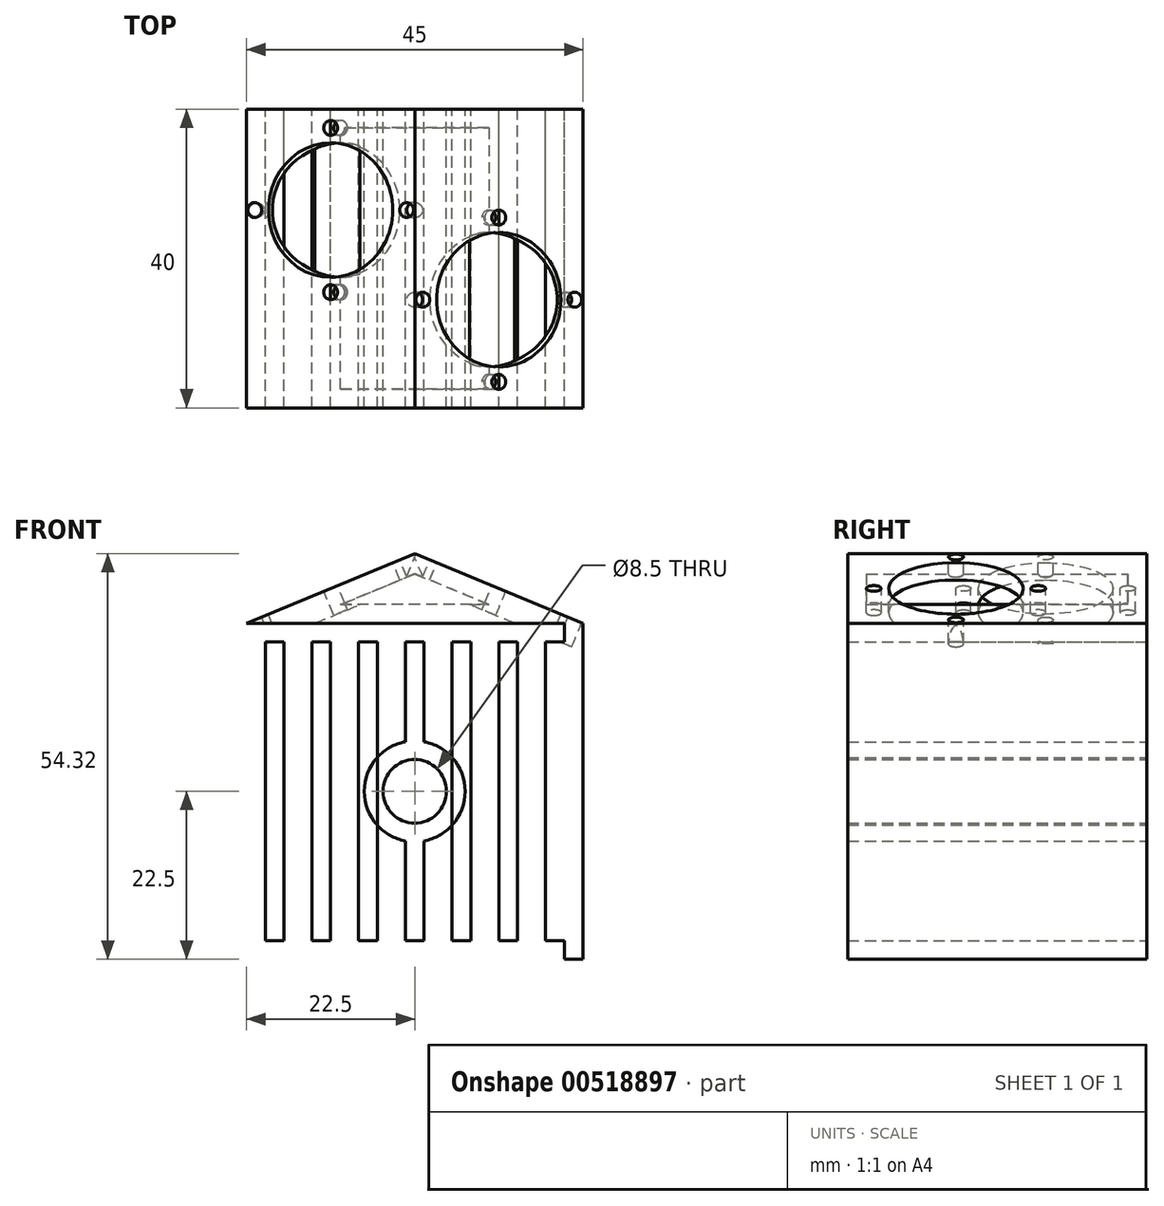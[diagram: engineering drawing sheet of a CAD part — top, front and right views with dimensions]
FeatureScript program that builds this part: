
annotation { "Feature Type Name" : "Feature", "Feature Type Description" : "" }
export const myFeature = defineFeature(function(context is Context, id is Id, definition is map)
    precondition{}
    {
        {
            var Q0;
            Q0=qCreatedBy(makeId("Front.planeOp"),FACE);
            var sketch = newSketch(context, id + "F0", { "sketchPlane" : qUnion([Q0])});
            skLineSegment(sketch, "E0.bottom", {"start": v(22.5, 22.5) * mm, "end": v(-22.5, 22.5) * mm});
            skLineSegment(sketch, "E0.top", {"start": v(22.5, -22.5) * mm, "end": v(-22.5, -22.5) * mm});
            skLineSegment(sketch, "E0.left", {"start": v(22.5, 22.5) * mm, "end": v(22.5, -22.5) * mm});
            skLineSegment(sketch, "E0.right", {"start": v(-22.5, 22.5) * mm, "end": v(-22.5, -22.5) * mm});
            skPoint(sketch, "E0.middle", {"position": v(0, 0) * mm});
            skLineSegment(sketch, "E1", {"start": v(-22.5, 22.5) * mm, "end": v(0, 31.82) * mm});
            skLineSegment(sketch, "E2", {"start": v(0, 31.82) * mm, "end": v(22.5, 22.5) * mm});
            skCircle(sketch, "E3", {"center": v(0, 0) * mm, "radius": 4.25 * mm});
            skLineSegment(sketch, "E4.bottom", {"start": v(22.5, 22.5) * mm, "end": v(20, 22.5) * mm});
            skLineSegment(sketch, "E4.top", {"start": v(22.5, 20) * mm, "end": v(20, 20) * mm});
            skLineSegment(sketch, "E4.left", {"start": v(22.5, 22.5) * mm, "end": v(22.5, 20) * mm});
            skLineSegment(sketch, "E4.right", {"start": v(20, 22.5) * mm, "end": v(20, 20) * mm});
            skLineSegment(sketch, "E5.bottom", {"start": v(22.5, -22.5) * mm, "end": v(20, -22.5) * mm});
            skLineSegment(sketch, "E5.top", {"start": v(22.5, -20) * mm, "end": v(20, -20) * mm});
            skLineSegment(sketch, "E5.left", {"start": v(22.5, -22.5) * mm, "end": v(22.5, -20) * mm});
            skLineSegment(sketch, "E5.right", {"start": v(20, -22.5) * mm, "end": v(20, -20) * mm});
            skPoint(sketch, "E6.oppositeSnap0", {"position": v(21.25, -20) * mm});
            skLineSegment(sketch, "E6.bottom", {"start": v(20, 20) * mm, "end": v(17.5, 20) * mm});
            skLineSegment(sketch, "E6.top", {"start": v(20, -20) * mm, "end": v(17.5, -20) * mm});
            skLineSegment(sketch, "E6.left", {"start": v(20, 20) * mm, "end": v(20, -20) * mm});
            skLineSegment(sketch, "E6.right", {"start": v(17.5, 20) * mm, "end": v(17.5, -20) * mm});
            skLineSegment(sketch, "E7.1.0.0", {"start": v(13.75, 20) * mm, "end": v(13.75, -20) * mm});
            skLineSegment(sketch, "E7.1.0.1", {"start": v(11.25, 20) * mm, "end": v(11.25, -20) * mm});
            skLineSegment(sketch, "E7.1.0.2", {"start": v(13.75, 20) * mm, "end": v(11.25, 20) * mm});
            skLineSegment(sketch, "E7.1.0.3", {"start": v(13.75, -20) * mm, "end": v(11.25, -20) * mm});
            skLineSegment(sketch, "E7.2.0.0", {"start": v(7.5, 20) * mm, "end": v(7.5, -20) * mm});
            skLineSegment(sketch, "E7.2.0.1", {"start": v(5, 20) * mm, "end": v(5, -20) * mm});
            skLineSegment(sketch, "E7.2.0.2", {"start": v(7.5, 20) * mm, "end": v(5, 20) * mm});
            skLineSegment(sketch, "E7.2.0.3", {"start": v(7.5, -20) * mm, "end": v(5, -20) * mm});
            skLineSegment(sketch, "E7.3.0.0", {"start": v(1.25, 20) * mm, "end": v(1.25, -20) * mm});
            skLineSegment(sketch, "E7.3.0.1", {"start": v(-1.25, 20) * mm, "end": v(-1.25, -20) * mm});
            skLineSegment(sketch, "E7.3.0.2", {"start": v(1.25, 20) * mm, "end": v(-1.25, 20) * mm});
            skLineSegment(sketch, "E7.3.0.3", {"start": v(1.25, -20) * mm, "end": v(-1.25, -20) * mm});
            skLineSegment(sketch, "E7.4.0.0", {"start": v(-5, 20) * mm, "end": v(-5, -20) * mm});
            skLineSegment(sketch, "E7.4.0.1", {"start": v(-7.5, 20) * mm, "end": v(-7.5, -20) * mm});
            skLineSegment(sketch, "E7.4.0.2", {"start": v(-5, 20) * mm, "end": v(-7.5, 20) * mm});
            skLineSegment(sketch, "E7.4.0.3", {"start": v(-5, -20) * mm, "end": v(-7.5, -20) * mm});
            skLineSegment(sketch, "E7.5.0.0", {"start": v(-11.25, 20) * mm, "end": v(-11.25, -20) * mm});
            skLineSegment(sketch, "E7.5.0.1", {"start": v(-13.75, 20) * mm, "end": v(-13.75, -20) * mm});
            skLineSegment(sketch, "E7.5.0.2", {"start": v(-11.25, 20) * mm, "end": v(-13.75, 20) * mm});
            skLineSegment(sketch, "E7.5.0.3", {"start": v(-11.25, -20) * mm, "end": v(-13.75, -20) * mm});
            skLineSegment(sketch, "E7.direction1", {"start": v(20, -20) * mm, "end": v(13.75, -20) * mm, "construction": true});
            skCircle(sketch, "E8", {"center": v(0, 0) * mm, "radius": 6.75 * mm});
            skLineSegment(sketch, "E9.0.6.0", {"start": v(-17.5, 20) * mm, "end": v(-17.5, -20) * mm});
            skLineSegment(sketch, "E9.3.6.0", {"start": v(-20, 20) * mm, "end": v(-20, -20) * mm});
            skLineSegment(sketch, "E9.6.6.0", {"start": v(-17.5, 20) * mm, "end": v(-20, 20) * mm});
            skLineSegment(sketch, "E9.9.6.0", {"start": v(-17.5, -20) * mm, "end": v(-20, -20) * mm});
            skSolve(sketch);
        }
        {
            var Q0;
            {var subQ0=sQuery(id+"F0.wireOp",EDGE,"E7.3.0.1");var subQ1=sQuery(id+"F0.wireOp",EDGE,"E3");var subQ2=makeQuery(id+"F0.imprint","INTERSECT",VERTEX,{"disambiguationData":[OD(0.0)],"derivedFrom":[subQ1,subQ0]});Q0=makeQuery(id+"F0.imprint","IMPRINT",FACE,{"disambiguationData":[TD([[makeQuery(id+"F0.imprint","IMPRINT",EDGE,{"disambiguationData":[TD([[subQ2,-1.0]])],"derivedFrom":subQ1}),1.0]])]});}
            var Q1;
            {var subQ0=sQuery(id+"F0.wireOp",EDGE,"E7.3.0.0");var subQ1=sQuery(id+"F0.wireOp",EDGE,"E3");var subQ2=makeQuery(id+"F0.imprint","INTERSECT",VERTEX,{"disambiguationData":[OD(0.0)],"derivedFrom":[subQ1,subQ0]});Q1=makeQuery(id+"F0.imprint","IMPRINT",FACE,{"disambiguationData":[TD([[makeQuery(id+"F0.imprint","IMPRINT",EDGE,{"disambiguationData":[TD([[subQ2,1.0]])],"derivedFrom":subQ1}),1.0]])]});}
            var Q2;
            Q2=makeQuery(id+"F0.imprint","IMPRINT",FACE,{"disambiguationData":[TD([[makeQuery(id+"F0.imprint","IMPRINT",EDGE,{"derivedFrom":sQuery(id+"F0.wireOp",EDGE,"E7.5.0.0")}),-1.0]])]});
            var Q3;
            Q3=makeQuery(id+"F0.imprint","IMPRINT",FACE,{"disambiguationData":[TD([[makeQuery(id+"F0.imprint","IMPRINT",EDGE,{"derivedFrom":sQuery(id+"F0.wireOp",EDGE,"E6.bottom")}),1.0]])]});
            var Q4;
            Q4=makeQuery(id+"F0.imprint","IMPRINT",FACE,{"disambiguationData":[TD([[makeQuery(id+"F0.imprint","IMPRINT",EDGE,{"derivedFrom":sQuery(id+"F0.wireOp",EDGE,"E7.2.0.0")}),-1.0]])]});
            var Q5;
            {var subQ0=sQuery(id+"F0.wireOp",EDGE,"E8");var subQ1=sQuery(id+"F0.wireOp",EDGE,"E7.2.0.1");var subQ2=makeQuery(id+"F0.imprint","INTERSECT",VERTEX,{"disambiguationData":[OD(0.0)],"derivedFrom":[subQ1,subQ0]});Q5=makeQuery(id+"F0.imprint","IMPRINT",FACE,{"disambiguationData":[TD([[makeQuery(id+"F0.imprint","IMPRINT",EDGE,{"disambiguationData":[TD([[subQ2,-1.0]])],"derivedFrom":subQ1}),1.0]])]});}
            var Q6;
            {var subQ0=sQuery(id+"F0.wireOp",EDGE,"E7.3.0.2");Q6=makeQuery(id+"F0.imprint","IMPRINT",FACE,{"disambiguationData":[TD([[makeQuery(id+"F0.imprint","IMPRINT",EDGE,{"derivedFrom":subQ0}),1.0]])]});}
            var Q7;
            {var subQ4=sQuery(id+"F0.wireOp",EDGE,"E7.3.0.1");var subQ6=sQuery(id+"F0.wireOp",EDGE,"E3");var subQ9=makeQuery(id+"F0.imprint","INTERSECT",VERTEX,{"disambiguationData":[OD(0.0)],"derivedFrom":[subQ6,subQ4]});Q7=makeQuery(id+"F0.imprint","IMPRINT",FACE,{"disambiguationData":[TD([[makeQuery(id+"F0.imprint","IMPRINT",EDGE,{"disambiguationData":[TD([[subQ9,-1.0]])],"derivedFrom":subQ6}),-1.0]])]});}
            var Q8;
            {var subQ0=sQuery(id+"F0.wireOp",EDGE,"E7.3.0.1");var subQ1=sQuery(id+"F0.wireOp",EDGE,"E3");var subQ2=makeQuery(id+"F0.imprint","INTERSECT",VERTEX,{"disambiguationData":[OD(1.0)],"derivedFrom":[subQ1,subQ0]});Q8=makeQuery(id+"F0.imprint","IMPRINT",FACE,{"disambiguationData":[TD([[makeQuery(id+"F0.imprint","IMPRINT",EDGE,{"disambiguationData":[TD([[subQ2,-1.0]])],"derivedFrom":subQ1}),-1.0]])]});}
            var Q9;
            {var subQ0=sQuery(id+"F0.wireOp",EDGE,"E7.3.0.0");var subQ1=sQuery(id+"F0.wireOp",EDGE,"E3");var subQ5=makeQuery(id+"F0.imprint","INTERSECT",VERTEX,{"disambiguationData":[OD(0.0)],"derivedFrom":[subQ1,subQ0]});Q9=makeQuery(id+"F0.imprint","IMPRINT",FACE,{"disambiguationData":[TD([[makeQuery(id+"F0.imprint","IMPRINT",EDGE,{"disambiguationData":[TD([[subQ5,1.0]])],"derivedFrom":subQ1}),-1.0]])]});}
            var Q10;
            {var subQ0=sQuery(id+"F0.wireOp",EDGE,"E7.3.0.1");var subQ1=sQuery(id+"F0.wireOp",EDGE,"E3");var subQ2=makeQuery(id+"F0.imprint","INTERSECT",VERTEX,{"disambiguationData":[OD(0.0)],"derivedFrom":[subQ1,subQ0]});Q10=makeQuery(id+"F0.imprint","IMPRINT",FACE,{"disambiguationData":[TD([[makeQuery(id+"F0.imprint","IMPRINT",EDGE,{"disambiguationData":[TD([[subQ2,1.0]])],"derivedFrom":subQ1}),-1.0]])]});}
            var Q11;
            {var subQ0=sQuery(id+"F0.wireOp",EDGE,"E8");var subQ1=sQuery(id+"F0.wireOp",EDGE,"E7.4.0.0");var subQ2=makeQuery(id+"F0.imprint","INTERSECT",VERTEX,{"disambiguationData":[OD(0.0)],"derivedFrom":[subQ1,subQ0]});Q11=makeQuery(id+"F0.imprint","IMPRINT",FACE,{"disambiguationData":[TD([[makeQuery(id+"F0.imprint","IMPRINT",EDGE,{"disambiguationData":[TD([[subQ2,-1.0]])],"derivedFrom":subQ1}),-1.0]])]});}
            var Q12;
            Q12=makeQuery(id+"F0.imprint","IMPRINT",FACE,{"disambiguationData":[TD([[makeQuery(id+"F0.imprint","IMPRINT",EDGE,{"derivedFrom":sQuery(id+"F0.wireOp",EDGE,"E7.4.0.1")}),1.0]])]});
            var Q13;
            Q13=makeQuery(id+"F0.imprint","IMPRINT",FACE,{"disambiguationData":[TD([[makeQuery(id+"F0.imprint","IMPRINT",EDGE,{"derivedFrom":sQuery(id+"F0.wireOp",EDGE,"E9.0.6.0")}),-1.0]])]});
            var Q14;
            Q14=makeQuery(id+"F0.imprint","IMPRINT",FACE,{"disambiguationData":[TD([[makeQuery(id+"F0.imprint","IMPRINT",EDGE,{"derivedFrom":sQuery(id+"F0.wireOp",EDGE,"E0.bottom")}),-1.0]])]});
            var Q15;
            Q15=makeQuery(id+"F0.imprint","IMPRINT",FACE,{"disambiguationData":[TD([[makeQuery(id+"F0.imprint","IMPRINT",EDGE,{"derivedFrom":sQuery(id+"F0.wireOp",EDGE,"E0.left")}),-1.0]])]});
            var Q16;
            {var subQ0=sQuery(id+"F0.wireOp",EDGE,"E7.3.0.1");var subQ1=sQuery(id+"F0.wireOp",EDGE,"E3");var subQ2=makeQuery(id+"F0.imprint","INTERSECT",VERTEX,{"disambiguationData":[OD(0.0)],"derivedFrom":[subQ1,subQ0]});Q16=makeQuery(id+"F0.imprint","IMPRINT",FACE,{"disambiguationData":[TD([[makeQuery(id+"F0.imprint","IMPRINT",EDGE,{"disambiguationData":[TD([[subQ2,1.0]])],"derivedFrom":subQ1}),1.0]])]});}
            var Q17;
            Q17=makeQuery(id+"F0.imprint","IMPRINT",FACE,{"disambiguationData":[TD([[makeQuery(id+"F0.imprint","IMPRINT",EDGE,{"derivedFrom":sQuery(id+"F0.wireOp",EDGE,"E5.bottom")}),-1.0]])]});
            var Q18;
            {var subQ0=sQuery(id+"F0.wireOp",EDGE,"E7.3.0.3");Q18=makeQuery(id+"F0.imprint","IMPRINT",FACE,{"disambiguationData":[TD([[makeQuery(id+"F0.imprint","IMPRINT",EDGE,{"derivedFrom":subQ0}),-1.0]])]});}
            var Q19;
            Q19=makeQuery(id+"F0.imprint","IMPRINT",FACE,{"disambiguationData":[TD([[makeQuery(id+"F0.imprint","IMPRINT",EDGE,{"derivedFrom":sQuery(id+"F0.wireOp",EDGE,"E7.1.0.0")}),-1.0]])]});
            var Q20;
            Q20=makeQuery(id+"F0.imprint","IMPRINT",FACE,{"disambiguationData":[TD([[makeQuery(id+"F0.imprint","IMPRINT",EDGE,{"derivedFrom":sQuery(id+"F0.wireOp",EDGE,"E0.bottom")}),1.0]])]});
            var Q21;
            Q21=makeQuery(id+"F0.imprint","IMPRINT",FACE,{"disambiguationData":[TD([[makeQuery(id+"F0.imprint","IMPRINT",EDGE,{"derivedFrom":sQuery(id+"F0.wireOp",EDGE,"E4.bottom")}),1.0]])]});
            extrude(context, id + "F1", {"entities" : qUnion([Q0, Q1, Q2, Q3, Q4, Q5, Q6, Q7, Q8, Q9, Q10, Q11, Q12, Q13, Q14, Q15, Q16, Q17, Q18, Q19, Q20, Q21]), "depth" : 40 * mm, "offsetDistance" : 25 * mm});
        }
        {
            var Q0;
            Q0=makeQuery(id+"F1.opExtrude","SWEPT_FACE",FACE,{"disambiguationData":[OSD([sQuery(id+"F0.wireOp",EDGE,"E0.top"),sQuery(id+"F0.wireOp",EDGE,"E5.bottom")])]});
            shell(context, id + "F2", {"entities" : qUnion([Q0]), "thickness" : 2.5 * mm});
        }
        {
            var Q0;
            {var subQ0=sQuery(id+"F0.wireOp",EDGE,"E7.3.0.0");var subQ1=sQuery(id+"F0.wireOp",EDGE,"E3");var subQ2=makeQuery(id+"F0.imprint","INTERSECT",VERTEX,{"disambiguationData":[OD(0.0)],"derivedFrom":[subQ1,subQ0]});Q0=makeQuery(id+"F0.imprint","IMPRINT",FACE,{"disambiguationData":[TD([[makeQuery(id+"F0.imprint","IMPRINT",EDGE,{"disambiguationData":[TD([[subQ2,1.0]])],"derivedFrom":subQ1}),1.0]])]});}
            var Q1;
            {var subQ0=sQuery(id+"F0.wireOp",EDGE,"E7.3.0.1");var subQ1=sQuery(id+"F0.wireOp",EDGE,"E3");var subQ2=makeQuery(id+"F0.imprint","INTERSECT",VERTEX,{"disambiguationData":[OD(0.0)],"derivedFrom":[subQ1,subQ0]});Q1=makeQuery(id+"F0.imprint","IMPRINT",FACE,{"disambiguationData":[TD([[makeQuery(id+"F0.imprint","IMPRINT",EDGE,{"disambiguationData":[TD([[subQ2,1.0]])],"derivedFrom":subQ1}),1.0]])]});}
            var Q2;
            {var subQ0=sQuery(id+"F0.wireOp",EDGE,"E7.3.0.1");var subQ1=sQuery(id+"F0.wireOp",EDGE,"E3");var subQ2=makeQuery(id+"F0.imprint","INTERSECT",VERTEX,{"disambiguationData":[OD(0.0)],"derivedFrom":[subQ1,subQ0]});Q2=makeQuery(id+"F0.imprint","IMPRINT",FACE,{"disambiguationData":[TD([[makeQuery(id+"F0.imprint","IMPRINT",EDGE,{"disambiguationData":[TD([[subQ2,-1.0]])],"derivedFrom":subQ1}),1.0]])]});}
            extrude(context, id + "F3", {"entities" : qUnion([Q0, Q1, Q2]), "operationType" : NewBodyOperationType.REMOVE, "depth" : 40 * mm, "offsetDistance" : 25 * mm});
        }
        {
            var Q0;
            Q0=makeQuery(id+"F1.opExtrude","SWEPT_FACE",FACE,{"disambiguationData":[OSD([sQuery(id+"F0.wireOp",EDGE,"E1")])]});
            var sketch = newSketch(context, id + "F4", { "sketchPlane" : qUnion([Q0])});
            skLineSegment(sketch, "E10", {"start": v(0, 0) * mm, "end": v(0, -13.5) * mm});
            skPoint(sketch, "E10.endSnap0", {"position": v(0, 0) * mm});
            skCircle(sketch, "E11", {"center": v(0, -13.5) * mm, "radius": 9 * mm});
            skLineSegment(sketch, "E12", {"start": v(0, -13.5) * mm, "end": v(-11, -13.5) * mm});
            skLineSegment(sketch, "E13", {"start": v(0, -13.5) * mm, "end": v(0, -24.5) * mm});
            skLineSegment(sketch, "E14", {"start": v(0, -13.5) * mm, "end": v(11, -13.5) * mm});
            skLineSegment(sketch, "E15", {"start": v(0, -13.5) * mm, "end": v(0, -2.5) * mm});
            skCircle(sketch, "E16", {"center": v(0, -24.5) * mm, "radius": 1 * mm});
            skCircle(sketch, "E17", {"center": v(-11, -13.5) * mm, "radius": 1 * mm});
            skCircle(sketch, "E18", {"center": v(11, -13.5) * mm, "radius": 1 * mm});
            skCircle(sketch, "E19", {"center": v(0, -2.5) * mm, "radius": 1 * mm});
            skSolve(sketch);
        }
        {
            var Q0;
            Q0=makeQuery(id+"F1.opExtrude","SWEPT_FACE",FACE,{"disambiguationData":[OSD([sQuery(id+"F0.wireOp",EDGE,"E2")])]});
            var sketch = newSketch(context, id + "F5", { "sketchPlane" : qUnion([Q0])});
            skLineSegment(sketch, "E20", {"start": v(0, -40) * mm, "end": v(0, -25.5) * mm});
            skPoint(sketch, "E20.endSnap0", {"position": v(0, -40) * mm});
            skCircle(sketch, "E21", {"center": v(0, -25.5) * mm, "radius": 9 * mm});
            skLineSegment(sketch, "E22", {"start": v(0, -25.5) * mm, "end": v(-11, -25.5) * mm});
            skLineSegment(sketch, "E23", {"start": v(0, -25.5) * mm, "end": v(11, -25.5) * mm});
            skLineSegment(sketch, "E24", {"start": v(0, -25.5) * mm, "end": v(0, -14.5) * mm});
            skLineSegment(sketch, "E25", {"start": v(0, -25.5) * mm, "end": v(0, -36.5) * mm});
            skCircle(sketch, "E26", {"center": v(-11, -25.5) * mm, "radius": 1 * mm});
            skCircle(sketch, "E27", {"center": v(0, -14.5) * mm, "radius": 1 * mm});
            skCircle(sketch, "E28", {"center": v(11, -25.5) * mm, "radius": 1 * mm});
            skCircle(sketch, "E29", {"center": v(0, -36.5) * mm, "radius": 1 * mm});
            skSolve(sketch);
        }
        {
            var Q0;
            Q0=makeQuery(id+"F5.imprint","IMPRINT",FACE,{"disambiguationData":[TD([[makeQuery(id+"F5.imprint","IMPRINT",EDGE,{"derivedFrom":sQuery(id+"F5.wireOp",EDGE,"E21")}),1.0]])]});
            var Q1;
            Q1=makeQuery(id+"F5.imprint","IMPRINT",FACE,{"disambiguationData":[TD([[makeQuery(id+"F5.imprint","IMPRINT",EDGE,{"derivedFrom":sQuery(id+"F5.wireOp",EDGE,"E26")}),1.0]])]});
            var Q2;
            Q2=makeQuery(id+"F5.imprint","IMPRINT",FACE,{"disambiguationData":[TD([[makeQuery(id+"F5.imprint","IMPRINT",EDGE,{"derivedFrom":sQuery(id+"F5.wireOp",EDGE,"E27")}),1.0]])]});
            var Q3;
            Q3=makeQuery(id+"F5.imprint","IMPRINT",FACE,{"disambiguationData":[TD([[makeQuery(id+"F5.imprint","IMPRINT",EDGE,{"derivedFrom":sQuery(id+"F5.wireOp",EDGE,"E28")}),1.0]])]});
            var Q4;
            {var subQ0=sQuery(id+"F5.wireOp",EDGE,"E25");var subQ1=sQuery(id+"F5.wireOp",EDGE,"E20");var subQ2=makeQuery(id+"F5.imprint","INTERSECT",VERTEX,{"derivedFrom":[subQ1,subQ0]});Q4=makeQuery(id+"F5.imprint","IMPRINT",FACE,{"disambiguationData":[TD([[makeQuery(id+"F5.imprint","IMPRINT",EDGE,{"disambiguationData":[TD([[subQ2,1.0]])],"derivedFrom":subQ1}),-1.0]])]});}
            var Q5;
            {var subQ0=sQuery(id+"F5.wireOp",EDGE,"E25");var subQ1=sQuery(id+"F5.wireOp",EDGE,"E20");var subQ2=makeQuery(id+"F5.imprint","INTERSECT",VERTEX,{"derivedFrom":[subQ1,subQ0]});Q5=makeQuery(id+"F5.imprint","IMPRINT",FACE,{"disambiguationData":[TD([[makeQuery(id+"F5.imprint","IMPRINT",EDGE,{"disambiguationData":[TD([[subQ2,1.0]])],"derivedFrom":subQ1}),1.0]])]});}
            extrude(context, id + "F6", {"entities" : qUnion([Q0, Q1, Q2, Q3, Q4, Q5]), "operationType" : NewBodyOperationType.REMOVE, "oppositeDirection" : true, "depth" : 3.5 * mm, "offsetDistance" : 25 * mm});
        }
        {
            var Q0;
            Q0=makeQuery(id+"F4.imprint","IMPRINT",FACE,{"disambiguationData":[TD([[makeQuery(id+"F4.imprint","IMPRINT",EDGE,{"derivedFrom":sQuery(id+"F4.wireOp",EDGE,"E11")}),1.0]])]});
            var Q1;
            {var subQ0=sQuery(id+"F4.wireOp",EDGE,"E15");var subQ1=sQuery(id+"F4.wireOp",EDGE,"E10");var subQ2=makeQuery(id+"F4.imprint","INTERSECT",VERTEX,{"derivedFrom":[subQ1,subQ0]});Q1=makeQuery(id+"F4.imprint","IMPRINT",FACE,{"disambiguationData":[TD([[makeQuery(id+"F4.imprint","IMPRINT",EDGE,{"disambiguationData":[TD([[subQ2,1.0]])],"derivedFrom":subQ1}),1.0]])]});}
            var Q2;
            {var subQ0=sQuery(id+"F4.wireOp",EDGE,"E15");var subQ1=sQuery(id+"F4.wireOp",EDGE,"E10");var subQ2=makeQuery(id+"F4.imprint","INTERSECT",VERTEX,{"derivedFrom":[subQ1,subQ0]});Q2=makeQuery(id+"F4.imprint","IMPRINT",FACE,{"disambiguationData":[TD([[makeQuery(id+"F4.imprint","IMPRINT",EDGE,{"disambiguationData":[TD([[subQ2,1.0]])],"derivedFrom":subQ1}),-1.0]])]});}
            var Q3;
            Q3=makeQuery(id+"F4.imprint","IMPRINT",FACE,{"disambiguationData":[TD([[makeQuery(id+"F4.imprint","IMPRINT",EDGE,{"derivedFrom":sQuery(id+"F4.wireOp",EDGE,"E17")}),1.0]])]});
            var Q4;
            Q4=makeQuery(id+"F4.imprint","IMPRINT",FACE,{"disambiguationData":[TD([[makeQuery(id+"F4.imprint","IMPRINT",EDGE,{"derivedFrom":sQuery(id+"F4.wireOp",EDGE,"E16")}),1.0]])]});
            var Q5;
            Q5=makeQuery(id+"F4.imprint","IMPRINT",FACE,{"disambiguationData":[TD([[makeQuery(id+"F4.imprint","IMPRINT",EDGE,{"derivedFrom":sQuery(id+"F4.wireOp",EDGE,"E18")}),1.0]])]});
            extrude(context, id + "F7", {"entities" : qUnion([Q0, Q1, Q2, Q3, Q4, Q5]), "operationType" : NewBodyOperationType.REMOVE, "oppositeDirection" : true, "depth" : 3.5 * mm, "offsetDistance" : 25 * mm});
        }
    });
